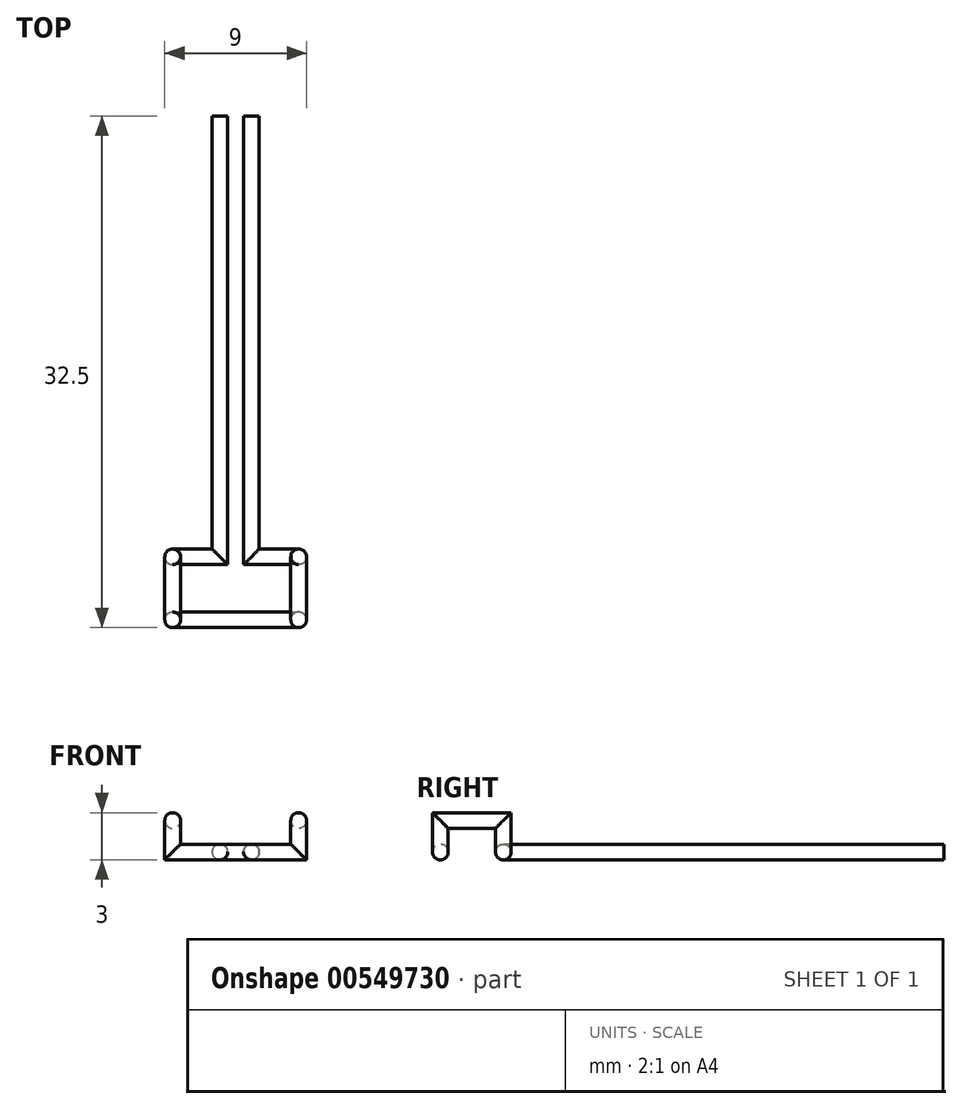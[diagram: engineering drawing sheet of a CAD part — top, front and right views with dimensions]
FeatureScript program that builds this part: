
annotation { "Feature Type Name" : "Feature", "Feature Type Description" : "" }
export const myFeature = defineFeature(function(context is Context, id is Id, definition is map)
    precondition{}
    {
        {
            var Q0;
            Q0=qCreatedBy(makeId("Top.planeOp"),FACE);
            var sketch = newSketch(context, id + "F0", { "sketchPlane" : qUnion([Q0])});
            skLineSegment(sketch, "E0", {"start": v(0, 30) * mm, "end": v(0, -2) * mm, "construction": true});
            skLineSegment(sketch, "E1.0", {"start": v(-1, 30) * mm, "end": v(-1, 2) * mm});
            skLineSegment(sketch, "E2", {"start": v(-5, 0) * mm, "end": v(5, 0) * mm, "construction": true});
            skLineSegment(sketch, "E3.0", {"start": v(-4, 2) * mm, "end": v(-1, 2) * mm});
            skLineSegment(sketch, "E4.0", {"start": v(-4, -2) * mm, "end": v(4, -2) * mm});
            skLineSegment(sketch, "E5.0", {"start": v(1, 30) * mm, "end": v(1, 2) * mm});
            skPoint(sketch, "E6.orphan", {"position": v(-73.98, 0) * mm});
            skPoint(sketch, "E7.orphan", {"position": v(0, 69.68) * mm});
            skLineSegment(sketch, "E8.trimOffspring", {"start": v(1, 2) * mm, "end": v(4, 2) * mm});
            skSolve(sketch);
        }
        {
            var Q0;
            Q0=qCreatedBy(makeId("Right.planeOp"),FACE);
            cPlane(context, id + "F1", {"entities" : qUnion([Q0]), "cplaneType" : CPlaneType.OFFSET, "offset" : 4 * mm, "width" : 150 * mm, "height" : 150 * mm});
        }
        {
            var Q0;
            Q0=qCreatedBy(id+"F1.planeOp",FACE);
            var sketch = newSketch(context, id + "F2", { "sketchPlane" : qUnion([Q0])});
            skLineSegment(sketch, "E9", {"start": v(2, 0) * mm, "end": v(2, 2) * mm});
            skLineSegment(sketch, "E10", {"start": v(-2, 2) * mm, "end": v(-2, 0) * mm});
            skLineSegment(sketch, "E11", {"start": v(2, 2) * mm, "end": v(-2, 2) * mm});
            skSolve(sketch);
        }
        {
            var Q0;
            Q0=qCreatedBy(makeId("Right.planeOp"),FACE);
            cPlane(context, id + "F3", {"entities" : qUnion([Q0]), "cplaneType" : CPlaneType.OFFSET, "offset" : 4 * mm, "oppositeDirection" : true, "width" : 150 * mm, "height" : 150 * mm});
        }
        {
            var Q0;
            Q0=qCreatedBy(id+"F3.planeOp",FACE);
            var sketch = newSketch(context, id + "F4", { "sketchPlane" : qUnion([Q0])});
            skLineSegment(sketch, "E12", {"start": v(2, 0) * mm, "end": v(2, 2) * mm});
            skLineSegment(sketch, "E13", {"start": v(2, 2) * mm, "end": v(-2, 2) * mm});
            skLineSegment(sketch, "E14", {"start": v(-2, 2) * mm, "end": v(-2, 0) * mm});
            skSolve(sketch);
        }
        {
            var Q0;
            Q0=qCreatedBy(makeId("Front.planeOp"),FACE);
            var Q1;
            Q1=sQuery(id+"F0.wireOp",VERTEX,"E0.start");
            cPlane(context, id + "F5", {"entities" : qUnion([Q0, Q1]), "cplaneType" : CPlaneType.PLANE_POINT, "offset" : 25 * mm, "width" : 150 * mm, "height" : 150 * mm});
        }
        {
            var Q0;
            Q0=qCreatedBy(id+"F5.planeOp",FACE);
            var sketch = newSketch(context, id + "F6", { "sketchPlane" : qUnion([Q0])});
            skCircle(sketch, "E15", {"center": v(-1, 0) * mm, "radius": 0.5 * mm});
            skSolve(sketch);
        }
        {
            var Q0;
            Q0=makeQuery(id+"F6.imprint","IMPRINT",FACE,{"disambiguationData":[TD([[makeQuery(id+"F6.imprint","IMPRINT",EDGE,{"derivedFrom":sQuery(id+"F6.wireOp",EDGE,"E15")}),1.0]])]});
            var Q1;
            Q1 = qConstructionFilter(qBodyType(qCreatedBy(id + "F0" ,EDGE), BodyType.WIRE), ConstructionObject.NO);
            var Q2;
            Q2 = qConstructionFilter(qBodyType(qCreatedBy(id + "F2" ,EDGE), BodyType.WIRE), ConstructionObject.NO);
            var Q3;
            Q3 = qConstructionFilter(qBodyType(qCreatedBy(id + "F4" ,EDGE), BodyType.WIRE), ConstructionObject.NO);
            sweep(context, id + "F7", {"profiles" : qUnion([Q0]), "path" : qUnion([Q1, Q2, Q3])});
        }
    });
